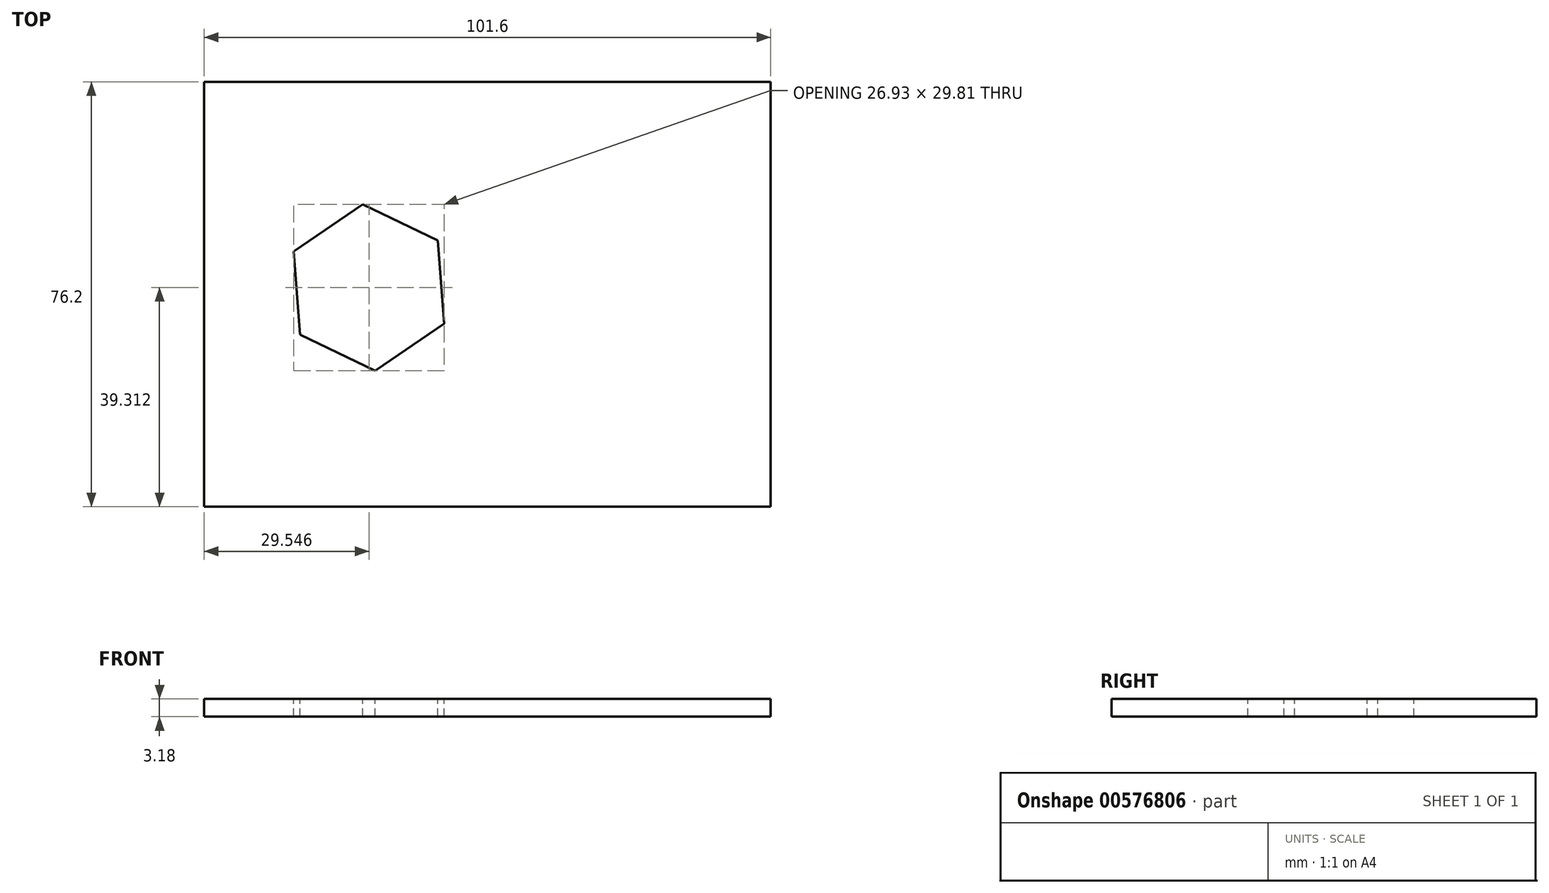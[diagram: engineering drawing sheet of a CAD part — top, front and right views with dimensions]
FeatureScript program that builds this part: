
annotation { "Feature Type Name" : "Feature", "Feature Type Description" : "" }
export const myFeature = defineFeature(function(context is Context, id is Id, definition is map)
    precondition{}
    {
        {
            var Q0;
            Q0=qCreatedBy(makeId("Top.planeOp"),FACE);
            var sketch = newSketch(context, id + "F0", { "sketchPlane" : qUnion([Q0])});
            skLineSegment(sketch, "E0.bottom", {"start": v(-50.8, 38.1) * mm, "end": v(50.8, 38.1) * mm});
            skLineSegment(sketch, "E0.top", {"start": v(-50.8, -38.1) * mm, "end": v(50.8, -38.1) * mm});
            skLineSegment(sketch, "E0.left", {"start": v(-50.8, 38.1) * mm, "end": v(-50.8, -38.1) * mm});
            skLineSegment(sketch, "E0.right", {"start": v(50.8, 38.1) * mm, "end": v(50.8, -38.1) * mm});
            skPoint(sketch, "E0.middle", {"position": v(0, 0) * mm});
            skSolve(sketch);
        }
        {
            var Q0;
            Q0=makeQuery(id+"F0.imprint","IMPRINT",FACE,{"disambiguationData":[TD([[makeQuery(id+"F0.imprint","IMPRINT",EDGE,{"derivedFrom":sQuery(id+"F0.wireOp",EDGE,"E0.bottom")}),-1.0]])]});
            extrude(context, id + "F1", {"entities" : qUnion([Q0]), "endBound" : BoundingType.SYMMETRIC, "depth" : 3.17 * mm, "offsetDistance" : 25.4 * mm});
        }
        {
            var Q0;
            Q0=makeQuery(id+"F1.opExtrude","CAP_FACE",FACE,{"disambiguationData":[OSD([sQuery(id+"F0.wireOp",EDGE,"E0.bottom"),sQuery(id+"F0.wireOp",EDGE,"E0.top"),sQuery(id+"F0.wireOp",EDGE,"E0.left"),sQuery(id+"F0.wireOp",EDGE,"E0.right")])],"isStart":false});
            var sketch = newSketch(context, id + "F2", { "sketchPlane" : qUnion([Q0])});
            skCircle(sketch, "E1.cCircle", {"center": v(-21.25, 1.21) * mm, "radius": 12.94 * mm, "construction": true});
            skLineSegment(sketch, "E1.0", {"start": v(-34.72, 7.7) * mm, "end": v(-22.37, 16.12) * mm});
            skLineSegment(sketch, "E1.1", {"start": v(-22.37, 16.12) * mm, "end": v(-8.9, 9.63) * mm});
            skLineSegment(sketch, "E1.2", {"start": v(-8.9, 9.63) * mm, "end": v(-7.79, -5.27) * mm});
            skLineSegment(sketch, "E1.3", {"start": v(-7.79, -5.27) * mm, "end": v(-20.14, -13.7) * mm});
            skLineSegment(sketch, "E1.4", {"start": v(-20.14, -13.7) * mm, "end": v(-33.6, -7.2) * mm});
            skLineSegment(sketch, "E1.5", {"start": v(-33.6, -7.2) * mm, "end": v(-34.72, 7.7) * mm});
            skPoint(sketch, "E1.0.midPoint", {"position": v(-28.55, 11.9) * mm});
            skSolve(sketch);
        }
        {
            var Q0;
            Q0 = qSketchRegion(id + "F2", true);
            extrude(context, id + "F3", {"entities" : qUnion([Q0]), "operationType" : NewBodyOperationType.REMOVE, "endBound" : BoundingType.THROUGH_ALL, "oppositeDirection" : true, "depth" : 25.4 * mm, "offsetDistance" : 25.4 * mm});
        }
    });
